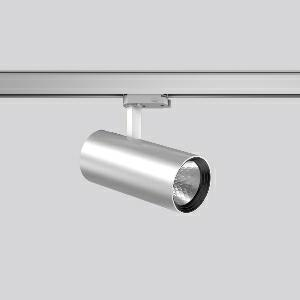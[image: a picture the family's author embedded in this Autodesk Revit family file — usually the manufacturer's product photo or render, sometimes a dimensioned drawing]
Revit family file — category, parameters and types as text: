
# Revit family: deecos_s_mini_742197_004_2_7344
name_source: partatom
category: Lighting Fixtures
units: mm (PartAtom-declared; Revit-internal decimal feet)

## family parameters
Cut with Voids When Loaded = No
Host = Face
Light Source = No
Part Type = Normal
Room Calculation Point = No
Round Connector Dimension = Use Diameter
Shared = No

## types (1)
- DEECOS S mini (1 x LED Modul 927, 2400 lm, 2700)
    Apparent Load = 20 VA
    Approval mark = CE
    CIE Flux Codes = 95 99 100 100 100
    Color Rendering = 92
    Color Temperature = 2700
    Default Elevation = 1800 mm
    Description = Series: DEECOS S mini
LED surface-mounted projector in modern design with no visible cooling ribs. Housing: die-cast aluminium, powder-coated. Rotation range: 356°. Swivel range: 90°. Black plastic ring and recessed LED to prevent glare from the side. Optical assembly with reflector made of MIRO-Silver with 98% total light reflection for outstanding efficiency - can be changed without tools. Best colour rendering index Ra>90. With multi adaptor for 3-circuit tracks 230 V. Suitable for Track on ceiling, Wall track. High quality converter without flickering and stroboscopic effect. The following accessories can be mounted without use of tools: interchangeable lenses, decorative glasses, honeycomb louvre, clear and frosted diffusers, white interchangeable plastic ring. 
Colour: silver
Diameter: 87 mm
Height: 214 mm
Lamp: LED
Socket: without socket
Colour temperature: 2700K
Colour rendering index (CRI): 92
System power: 20 W
Rated luminous flux: 2400 lm
Luminous efficiency: 120 lm/W
Control gear: Regulated power supply
Protection class: I
Type of protection: IP 20
    Height = 214 mm
    Lamp = 1 x LED Modul 927
    Lamp Light Flux = 2400 lm
    Lamp count = 1
    Length = 87 mm
    Lifetime = 50000 h
    Luminous efficacy = 120 lm/W
    Manufacturer = RZB
    ModVariant = No
    Model = 742197.004.2
    Mounting Place = Ceiling
    Mounting Type = Rail mounted
    Number of Poles = 1
    OnlyDefault = Yes
    Power Factor = 1
    Product Name = DEECOS S mini
    Product group = Track mounted projectors
    ProductGroupID = 301
    Protection Class = Protection class I
    Protection Degree = IP 20
    RLX_Detail_Level = 1
    RLX_Emergency_Light_Flux = 0 lm
    RLX_Emergency_Type = 0
    RLX_Emergency_Type_DB = No
    RlxData = <blob elided: 37085 chars, md5=396d2c7f>
    Socket = socket
    Standby Power = 0 W
    System Light Flux = 2400 lm
    System Power = 20 W
    Type Comments = Product without accessories
    Type Image = 741926.004.jpg
    URL = http://relux.com
    VarID = ---
    Voltage = 230 V
    Voltage Range = 220-240 V
    Weight = 0.00 kg
    Width = 0 mm  [stored 0 ft]

note: [stored X ft] marks values corroborated as IEEE doubles in the binary element streams (Revit-internal decimal feet)

## geometry (parser evidence)
native form markers: Blend x4, Sweep x13
no freeform markers — native parametric forms only
